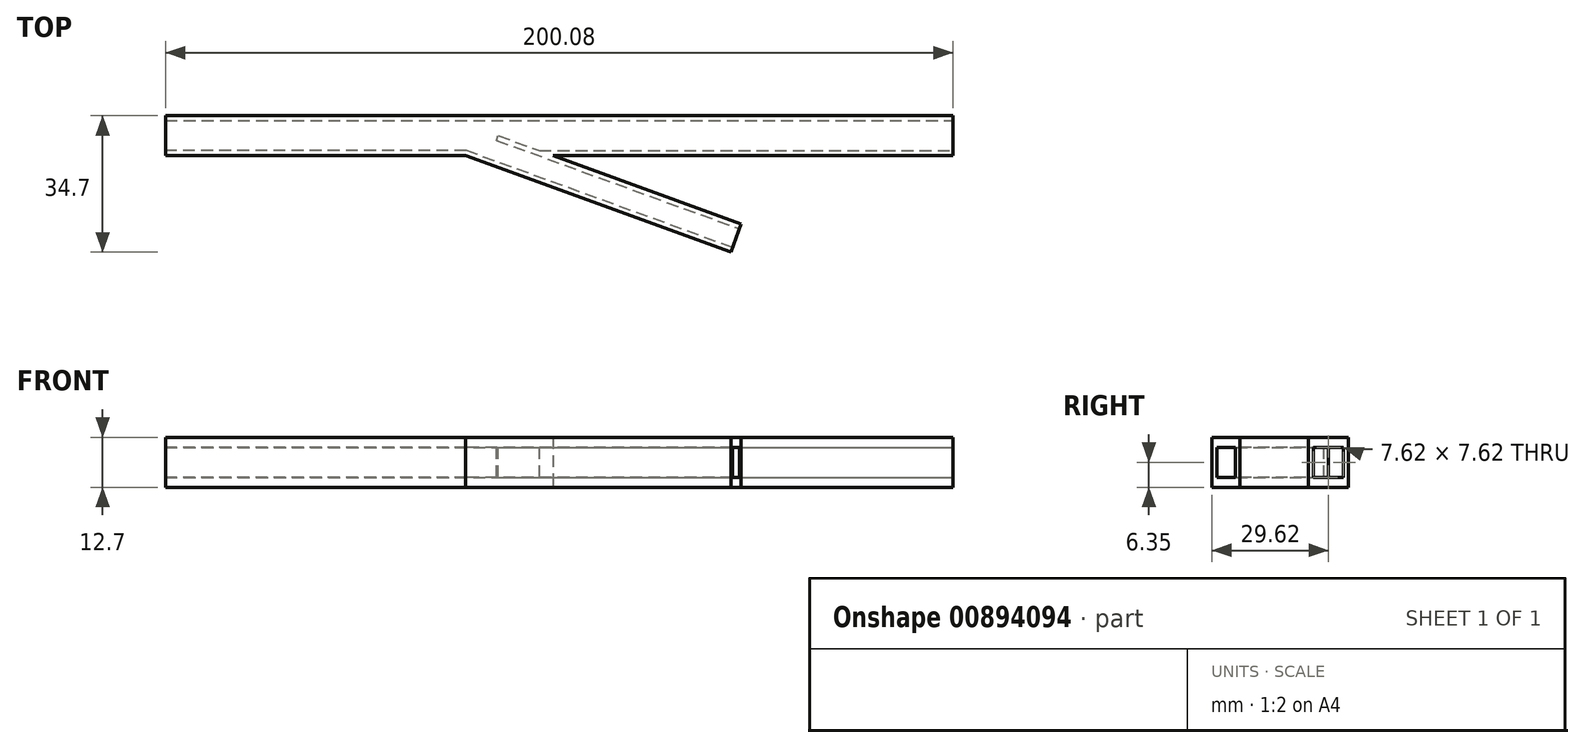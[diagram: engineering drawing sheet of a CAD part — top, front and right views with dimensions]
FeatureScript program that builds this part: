
annotation { "Feature Type Name" : "Feature", "Feature Type Description" : "" }
export const myFeature = defineFeature(function(context is Context, id is Id, definition is map)
    precondition{}
    {
        {
            var Q0;
            Q0=qCreatedBy(makeId("Top.planeOp"),FACE);
            var sketch = newSketch(context, id + "F0", { "sketchPlane" : qUnion([Q0])});
            skLineSegment(sketch, "E0", {"start": v(0, 0) * mm, "end": v(-101.6, 0) * mm});
            skLineSegment(sketch, "E1", {"start": v(-101.6, 0) * mm, "end": v(-53.86, -17.37) * mm});
            skLineSegment(sketch, "E2", {"start": v(-53.86, -17.37) * mm, "end": v(-56.47, -24.54) * mm});
            skLineSegment(sketch, "E3", {"start": v(-56.47, -24.54) * mm, "end": v(-123.88, 0) * mm});
            skLineSegment(sketch, "E4", {"start": v(-123.88, 0) * mm, "end": v(-200.08, 0) * mm});
            skLineSegment(sketch, "E5", {"start": v(-200.08, 0) * mm, "end": v(-200.08, 10.16) * mm});
            skLineSegment(sketch, "E6", {"start": v(-200.08, 10.16) * mm, "end": v(0, 10.16) * mm});
            skLineSegment(sketch, "E7", {"start": v(0, 10.16) * mm, "end": v(0, 0) * mm});
            skSolve(sketch);
        }
        {
            var Q0;
            Q0=makeQuery(id+"F0.imprint","IMPRINT",FACE,{"disambiguationData":[TD([[makeQuery(id+"F0.imprint","IMPRINT",EDGE,{"derivedFrom":sQuery(id+"F0.wireOp",EDGE,"E0")}),-1.0]])]});
            extrude(context, id + "F1", {"entities" : qUnion([Q0]), "depth" : 10.16 * mm, "offsetDistance" : 25.4 * mm});
        }
        {
            var Q0;
            Q0=makeQuery(id+"F1.opExtrude","CAP_FACE",FACE,{"disambiguationData":[OSD([sQuery(id+"F0.wireOp",EDGE,"E0"),sQuery(id+"F0.wireOp",EDGE,"E1"),sQuery(id+"F0.wireOp",EDGE,"E2"),sQuery(id+"F0.wireOp",EDGE,"E3"),sQuery(id+"F0.wireOp",EDGE,"E4"),sQuery(id+"F0.wireOp",EDGE,"E5"),sQuery(id+"F0.wireOp",EDGE,"E6"),sQuery(id+"F0.wireOp",EDGE,"E7")])],"isStart":false});
            var sketch = newSketch(context, id + "F2", { "sketchPlane" : qUnion([Q0])});
            skLineSegment(sketch, "E8", {"start": v(-116, 3.89) * mm, "end": v(-54.3, -18.57) * mm});
            skLineSegment(sketch, "E9", {"start": v(-56.04, -23.34) * mm, "end": v(-123.66, 1.27) * mm});
            skLineSegment(sketch, "E10", {"start": v(-123.66, 1.27) * mm, "end": v(-200.08, 1.27) * mm});
            skLineSegment(sketch, "E11", {"start": v(-200.08, 8.89) * mm, "end": v(0, 8.9) * mm});
            skLineSegment(sketch, "E12", {"start": v(-116, 3.89) * mm, "end": v(-115.56, 5.08) * mm});
            skLineSegment(sketch, "E13", {"start": v(-115.56, 5.08) * mm, "end": v(-105.09, 1.27) * mm});
            skLineSegment(sketch, "E14", {"start": v(-105.09, 1.27) * mm, "end": v(0, 1.27) * mm});
            skSolve(sketch);
        }
        {
            var Q0;
            {var subQ1=sQuery(id+"F2.wireOp",EDGE,"E8");Q0=makeQuery(id+"F2.imprint","IMPRINT",FACE,{"disambiguationData":[TD([[makeQuery(id+"F2.imprint","IMPRINT",EDGE,{"derivedFrom":subQ1}),-1.0]])]});}
            extrude(context, id + "F3", {"entities" : qUnion([Q0]), "operationType" : NewBodyOperationType.REMOVE, "oppositeDirection" : true, "depth" : 7.62 * mm, "offsetDistance" : 25.4 * mm});
        }
        {
            var Q0;
            {var subQ0=sQuery(id+"F0.wireOp",EDGE,"E5");var subQ1=sQuery(id+"F0.wireOp",EDGE,"E4");var subQ2=sQuery(id+"F0.wireOp",EDGE,"E3");var subQ3=sQuery(id+"F0.wireOp",EDGE,"E2");Q0=makeQuery(id+"F3.boolean.opBoolean","SPLIT",FACE,{"disambiguationData":[TD([makeQuery(id+"F1.opExtrude","SWEPT_FACE",FACE,{"disambiguationData":[OSD([subQ2])]})])],"derivedFrom":makeQuery(id+"F1.opExtrude","CAP_FACE",FACE,{"disambiguationData":[OSD([sQuery(id+"F0.wireOp",EDGE,"E0"),sQuery(id+"F0.wireOp",EDGE,"E1"),subQ3,subQ2,subQ1,subQ0,sQuery(id+"F0.wireOp",EDGE,"E6"),sQuery(id+"F0.wireOp",EDGE,"E7")])],"isStart":false})});}
            var sketch = newSketch(context, id + "F4", { "sketchPlane" : qUnion([Q0])});
            skLineSegment(sketch, "E15", {"start": v(0, 0) * mm, "end": v(-101.6, 0) * mm});
            skLineSegment(sketch, "E16", {"start": v(-101.6, 0) * mm, "end": v(-53.86, -17.37) * mm});
            skLineSegment(sketch, "E17", {"start": v(-53.86, -17.37) * mm, "end": v(-56.47, -24.54) * mm});
            skLineSegment(sketch, "E18", {"start": v(-56.47, -24.54) * mm, "end": v(-123.88, 0) * mm});
            skLineSegment(sketch, "E19", {"start": v(-123.88, 0) * mm, "end": v(-200.08, 0) * mm});
            skLineSegment(sketch, "E20", {"start": v(-200.08, 0) * mm, "end": v(-200.08, 10.16) * mm});
            skLineSegment(sketch, "E21", {"start": v(-200.08, 10.16) * mm, "end": v(0, 10.16) * mm});
            skLineSegment(sketch, "E22", {"start": v(0, 10.16) * mm, "end": v(0, 0) * mm});
            skSolve(sketch);
        }
        {
            var Q0;
            Q0 = qSketchRegion(id + "F4", true);
            extrude(context, id + "F5", {"entities" : qUnion([Q0]), "operationType" : NewBodyOperationType.ADD, "depth" : 2.54 * mm, "offsetDistance" : 25.4 * mm});
        }
    });
